# Revit family: DAL_A3-Sliding-Single-with-Sidehung-Sidelights
name_source: partatom
category: Doors
revit_build: Autodesk Revit 2016 (Build: 20150220_1215(x64)
units: mm (PartAtom-declared; Revit-internal decimal feet)

## family parameters
Always vertical = Yes
Cut with Voids When Loaded = No
Host = Wall
Room Calculation Point = No
Shared = No

## types (4) — shared parameters
Construction Type = Aluminium
Frame Finish = Anodised Aluminium
Function = Interior
Height = 2125 mm  [stored 6.97178 ft]
Manufacturer = Kal-Aluminium
Material Door Frame = Default Aluminium Door Frame
Material Glass = Glass
Model = Arcadia Patio Doors
Model Type = Double Sliding
URL = http://www.kal.co.za
Wall Closure = By host
window = 600 mm
zero-valued in all types: Rough Height, Rough Width, Thickness

## per-type parameters (varying)
| type | Description | Width | door width |
| 1500-600 | 1500mm WIDE ALUMINIUM SLIDING DOOR WITH 600mm WIDE SIDEHUNG SIDELIGHTS | 2700 mm  [stored 8.85827 ft] | 1500 mm  [stored 4.92126 ft] |
| 1800-600 | 1800mm WIDE ALUMINIUM SLIDING DOOR WITH 600mm WIDE SIDEHUNG SIDELIGHTS | 3000 mm  [stored 9.84252 ft] | 1800 mm  [stored 5.90551 ft] |
| 2100-600 | 2100mm WIDE ALUMINIUM SLIDING DOOR WITH 600mm WIDE SIDEHUNG SIDELIGHTS | 3300 mm  [stored 10.8268 ft] | 2100 mm |
| 2400-600 | 2400mm WIDE ALUMINIUM SLIDING DOOR WITH 600mm WIDE SIDEHUNG SIDELIGHTS | 3600 mm  [stored 11.811 ft] | 2400 mm |

note: [stored X ft] marks values corroborated as IEEE doubles in the binary element streams (Revit-internal decimal feet)

## geometry (parser evidence)
native form markers: Sweep x6
no freeform markers — native parametric forms only
